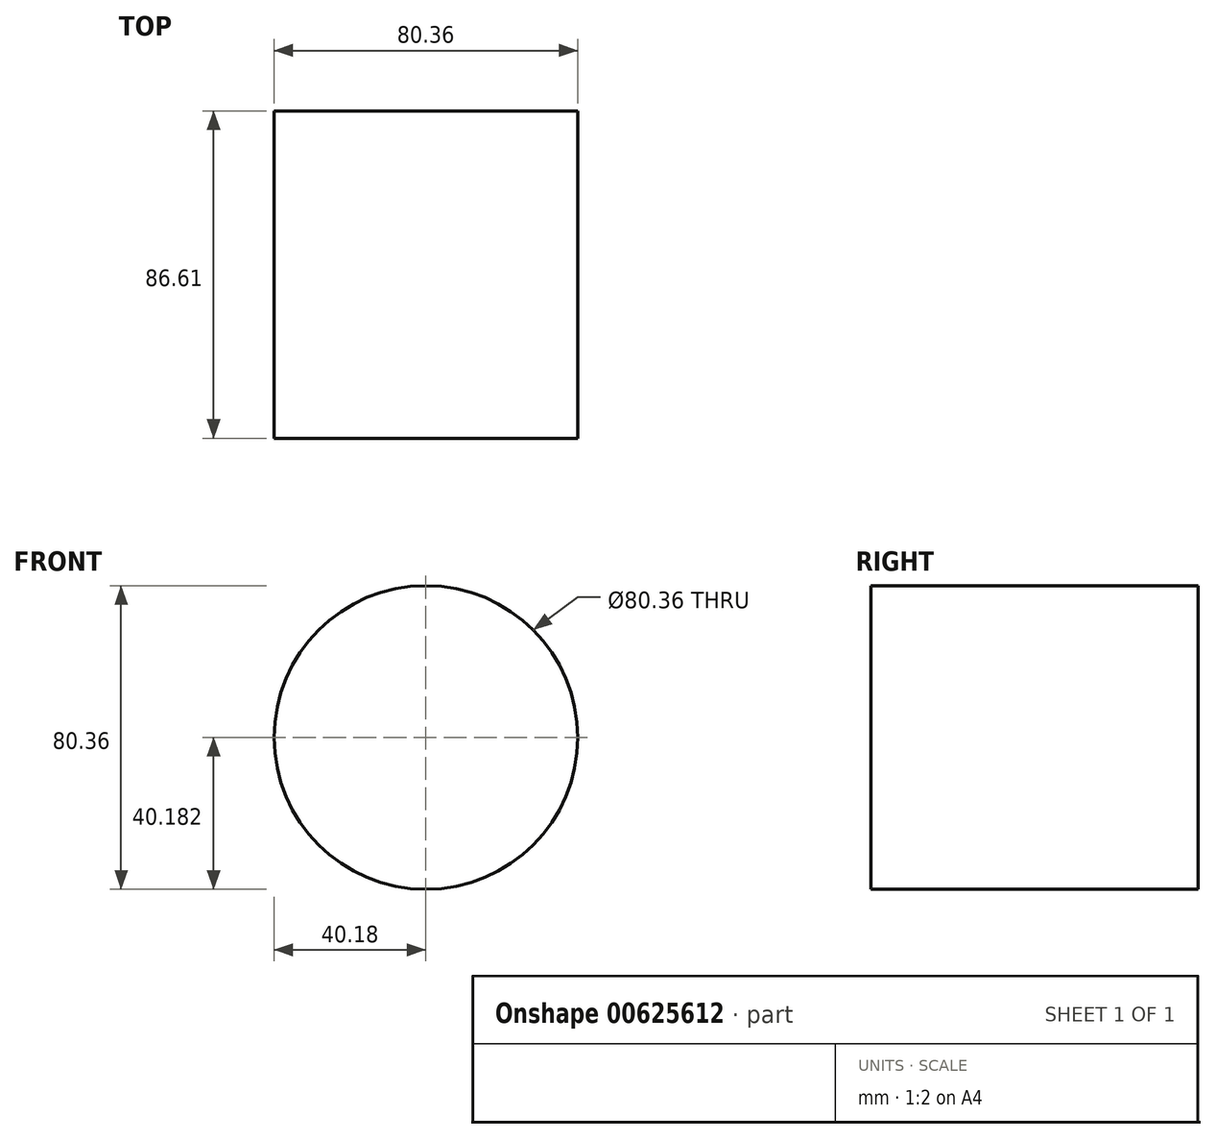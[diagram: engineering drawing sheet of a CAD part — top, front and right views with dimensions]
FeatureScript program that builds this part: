
annotation { "Feature Type Name" : "Feature", "Feature Type Description" : "" }
export const myFeature = defineFeature(function(context is Context, id is Id, definition is map)
    precondition{}
    {
        {
            var Q0;
            Q0=qCreatedBy(makeId("Front.planeOp"),FACE);
            var sketch = newSketch(context, id + "F0", { "sketchPlane" : qUnion([Q0])});
            skCircle(sketch, "E0", {"center": v(0, -10.55) * mm, "radius": 40.18 * mm});
            skSolve(sketch);
        }
        {
            var Q0;
            Q0=sQuery(id+"F0.wireOp",EDGE,"E0");
            extrude(context, id + "F1", {"bodyType" : ToolBodyType.SURFACE, "surfaceEntities" : qUnion([Q0]), "oppositeDirection" : true, "depth" : 86.61 * mm, "offsetDistance" : 25.4 * mm});
        }
    });
